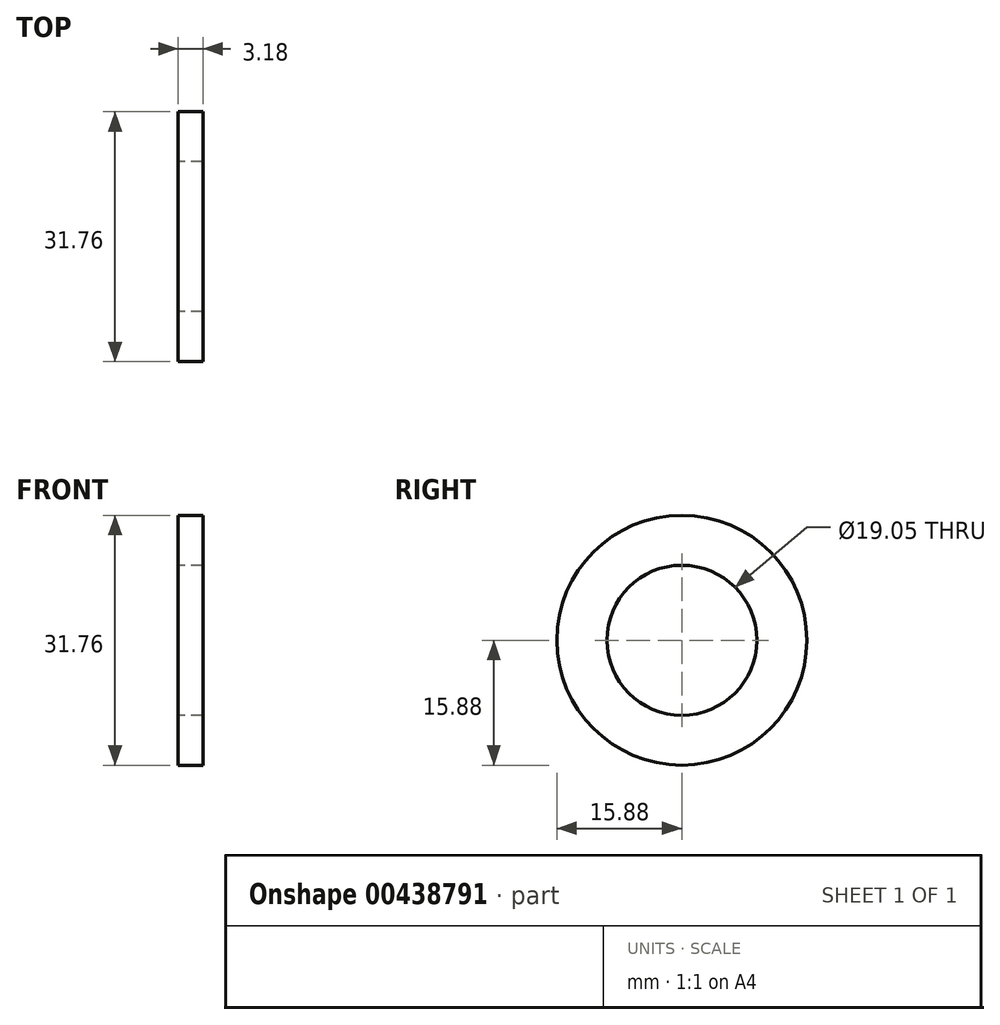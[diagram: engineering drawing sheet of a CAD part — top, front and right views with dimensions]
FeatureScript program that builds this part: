
annotation { "Feature Type Name" : "Feature", "Feature Type Description" : "" }
export const myFeature = defineFeature(function(context is Context, id is Id, definition is map)
    precondition{}
    {
        {
            var Q0;
            Q0=qCreatedBy(makeId("Right.planeOp"),FACE);
            var sketch = newSketch(context, id + "F0", { "sketchPlane" : qUnion([Q0])});
            skCircle(sketch, "E0", {"center": v(0, 0) * mm, "radius": 9.53 * mm});
            skCircle(sketch, "E1", {"center": v(0, 0) * mm, "radius": 15.88 * mm});
            skSolve(sketch);
        }
        {
            var Q0;
            Q0 = qSketchRegion(id + "F0", true);
            extrude(context, id + "F1", {"entities" : qUnion([Q0]), "depth" : 3.17 * mm});
        }
    });
